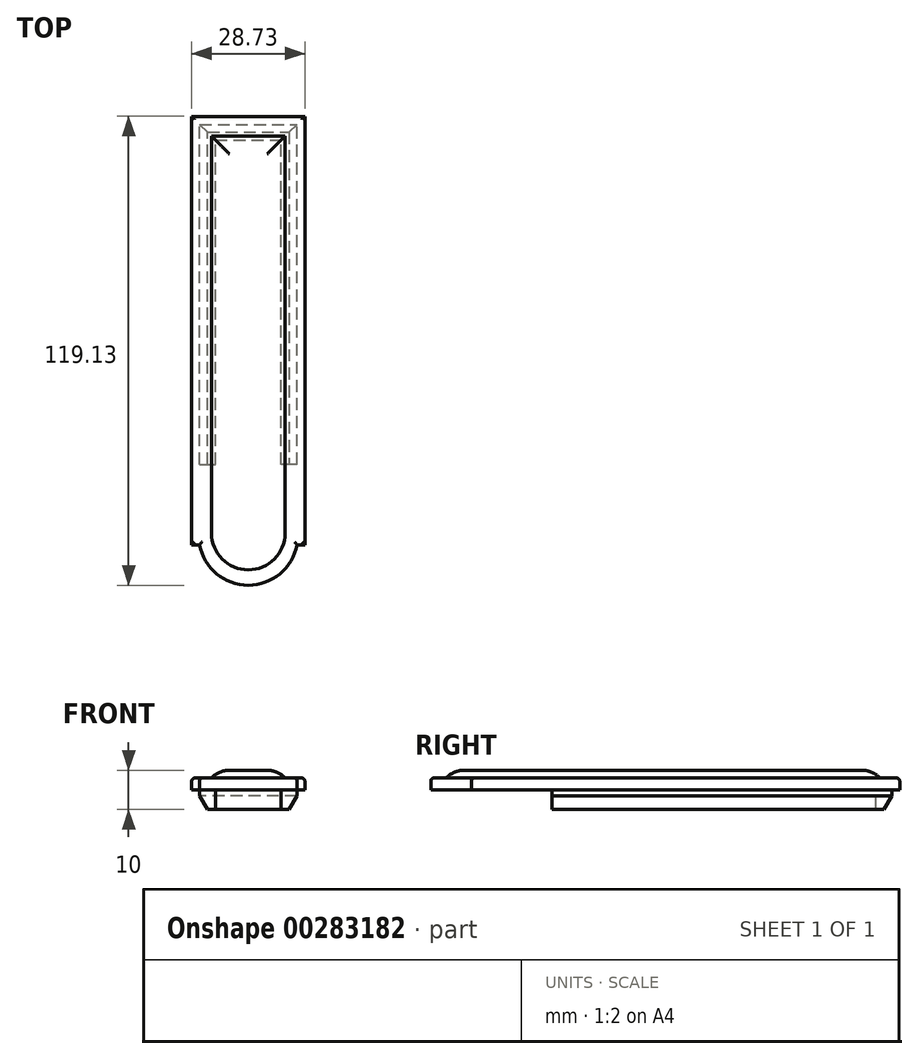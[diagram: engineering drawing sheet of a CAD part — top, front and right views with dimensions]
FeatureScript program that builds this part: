
annotation { "Feature Type Name" : "Feature", "Feature Type Description" : "" }
export const myFeature = defineFeature(function(context is Context, id is Id, definition is map)
    precondition{}
    {
        {
            var Q0;
            Q0=qCreatedBy(makeId("Top.planeOp"),FACE);
            var sketch = newSketch(context, id + "F0", { "sketchPlane" : qUnion([Q0])});
            skLineSegment(sketch, "E0.top", {"start": v(0, 108.84) * mm, "end": v(28.73, 108.84) * mm});
            skLineSegment(sketch, "E0.left", {"start": v(0, 0) * mm, "end": v(0, 108.84) * mm});
            skLineSegment(sketch, "E0.right", {"start": v(28.73, 0) * mm, "end": v(28.73, 108.84) * mm});
            skLineSegment(sketch, "E1", {"start": v(0, 0) * mm, "end": v(1.98, 0) * mm});
            skLineSegment(sketch, "E2", {"start": v(28.73, 0) * mm, "end": v(26.75, 0) * mm});
            skArc(sketch, "E3", {"start": v(1.98, 0) * mm, "mid": v(14.36, -10.29) * mm, "end": v(26.75, 0) * mm});
            skSolve(sketch);
        }
        {
            var Q0;
            Q0 = qSketchRegion(id + "F0", true);
            extrude(context, id + "F1", {"entities" : qUnion([Q0]), "depth" : 3 * mm});
        }
        {
            var Q0;
            Q0=makeQuery(id+"F1.opExtrude","CAP_FACE",FACE,{"disambiguationData":[OSD([sQuery(id+"F0.wireOp",EDGE,"E0.top"),sQuery(id+"F0.wireOp",EDGE,"E0.left"),sQuery(id+"F0.wireOp",EDGE,"E0.right"),sQuery(id+"F0.wireOp",EDGE,"ead56239-5c93-406e-bd90-1876c649dca1")])],"isStart":true});
            var sketch = newSketch(context, id + "F2", { "sketchPlane" : qUnion([Q0])});
            skLineSegment(sketch, "E4.0", {"start": v(2.03, -20.45) * mm, "end": v(2.03, -106.8) * mm});
            skLineSegment(sketch, "E4.1", {"start": v(26.7, -20.45) * mm, "end": v(26.7, -106.8) * mm});
            skLineSegment(sketch, "E4.2", {"start": v(26.7, -20.45) * mm, "end": v(22.7, -20.45) * mm});
            skLineSegment(sketch, "E4.3", {"start": v(2.03, -106.8) * mm, "end": v(26.7, -106.8) * mm});
            skLineSegment(sketch, "E4.5", {"start": v(2.03, -20.45) * mm, "end": v(6.03, -20.45) * mm});
            skLineSegment(sketch, "E5.0", {"start": v(22.7, -20.45) * mm, "end": v(22.7, -102.8) * mm});
            skLineSegment(sketch, "E5.1", {"start": v(6.03, -102.8) * mm, "end": v(22.7, -102.8) * mm});
            skLineSegment(sketch, "E5.2", {"start": v(6.03, -20.45) * mm, "end": v(6.03, -102.8) * mm});
            skSolve(sketch);
        }
        {
            var Q0;
            Q0 = qSketchRegion(id + "F2", true);
            extrude(context, id + "F3", {"entities" : qUnion([Q0]), "operationType" : NewBodyOperationType.ADD, "depth" : 5 * mm});
        }
        {
            var Q0;
            Q0=makeQuery(id+"F3.opExtrude","CAP_EDGE",EDGE,{"disambiguationData":[OSD([sQuery(id+"F2.wireOp",EDGE,"E4.0")])],"isStart":false});
            var Q1;
            Q1=makeQuery(id+"F3.opExtrude","CAP_EDGE",EDGE,{"disambiguationData":[OSD([sQuery(id+"F2.wireOp",EDGE,"E4.3")])],"isStart":false});
            var Q2;
            Q2=makeQuery(id+"F3.opExtrude","CAP_EDGE",EDGE,{"disambiguationData":[OSD([sQuery(id+"F2.wireOp",EDGE,"E4.1")])],"isStart":false});
            chamfer(context, id + "F4", {"entities" : qUnion([Q0, Q1, Q2]), "chamferType" : ChamferType.OFFSET_ANGLE, "width" : 2 * mm, "oppositeDirection" : false, "angle" : 60 * degree, "tangentPropagation" : true});
        }
        {
            var Q0;
            Q0=makeQuery(id+"F1.opExtrude","CAP_FACE",FACE,{"disambiguationData":[OSD([sQuery(id+"F0.wireOp",EDGE,"E0.top"),sQuery(id+"F0.wireOp",EDGE,"E0.left"),sQuery(id+"F0.wireOp",EDGE,"E0.right"),sQuery(id+"F0.wireOp",EDGE,"E1"),sQuery(id+"F0.wireOp",EDGE,"E2"),sQuery(id+"F0.wireOp",EDGE,"E3")])],"isStart":false});
            var sketch = newSketch(context, id + "F5", { "sketchPlane" : qUnion([Q0])});
            skLineSegment(sketch, "E6.1", {"start": v(5, 103.84) * mm, "end": v(23.73, 103.84) * mm});
            skLineSegment(sketch, "E6.2", {"start": v(23.73, 2.97) * mm, "end": v(23.73, 103.84) * mm});
            skLineSegment(sketch, "E6.3", {"start": v(5, 2.97) * mm, "end": v(5, 103.84) * mm});
            skArc(sketch, "E7", {"start": v(5, 2.97) * mm, "mid": v(14.36, -6.4) * mm, "end": v(23.73, 2.97) * mm});
            skSolve(sketch);
        }
        {
            var Q0;
            Q0 = qSketchRegion(id + "F5", true);
            extrude(context, id + "F6", {"entities" : qUnion([Q0]), "operationType" : NewBodyOperationType.ADD, "depth" : 2 * mm, "hasDraft" : true, "draftAngle" : 25 * degree, "draftPullDirection" : true});
        }
        {
            var Q0;
            Q0=makeQuery(id+"F6.opExtrude","CAP_FACE",FACE,{"disambiguationData":[OSD([sQuery(id+"F5.wireOp",EDGE,"E6.1"),sQuery(id+"F5.wireOp",EDGE,"E6.2"),sQuery(id+"F5.wireOp",EDGE,"E6.3"),sQuery(id+"F5.wireOp",EDGE,"E7")])],"isStart":false});
            fillet(context, id + "F7", {"entities" : qUnion([Q0]), "radius" : 6.35 * mm, "tangentPropagation" : true, "allowEdgeOverflow" : false});
        }
        {
            var Q0;
            Q0=makeQuery(id+"F1.opExtrude","CAP_EDGE",EDGE,{"disambiguationData":[OSD([sQuery(id+"F0.wireOp",EDGE,"E0.left")])],"isStart":false});
            var Q1;
            Q1=makeQuery(id+"F1.opExtrude","CAP_EDGE",EDGE,{"disambiguationData":[OSD([sQuery(id+"F0.wireOp",EDGE,"E1")])],"isStart":false});
            var Q2;
            Q2=makeQuery(id+"F1.opExtrude","CAP_EDGE",EDGE,{"disambiguationData":[OSD([sQuery(id+"F0.wireOp",EDGE,"E3")])],"isStart":false});
            var Q3;
            Q3=makeQuery(id+"F1.opExtrude","CAP_EDGE",EDGE,{"disambiguationData":[OSD([sQuery(id+"F0.wireOp",EDGE,"E2")])],"isStart":false});
            var Q4;
            Q4=makeQuery(id+"F1.opExtrude","CAP_EDGE",EDGE,{"disambiguationData":[OSD([sQuery(id+"F0.wireOp",EDGE,"E0.right")])],"isStart":false});
            var Q5;
            Q5=makeQuery(id+"F1.opExtrude","CAP_EDGE",EDGE,{"disambiguationData":[OSD([sQuery(id+"F0.wireOp",EDGE,"E0.top")])],"isStart":false});
            fillet(context, id + "F8", {"entities" : qUnion([Q0, Q1, Q2, Q3, Q4, Q5]), "radius" : 0.76 * mm, "tangentPropagation" : true, "allowEdgeOverflow" : false});
        }
    });
